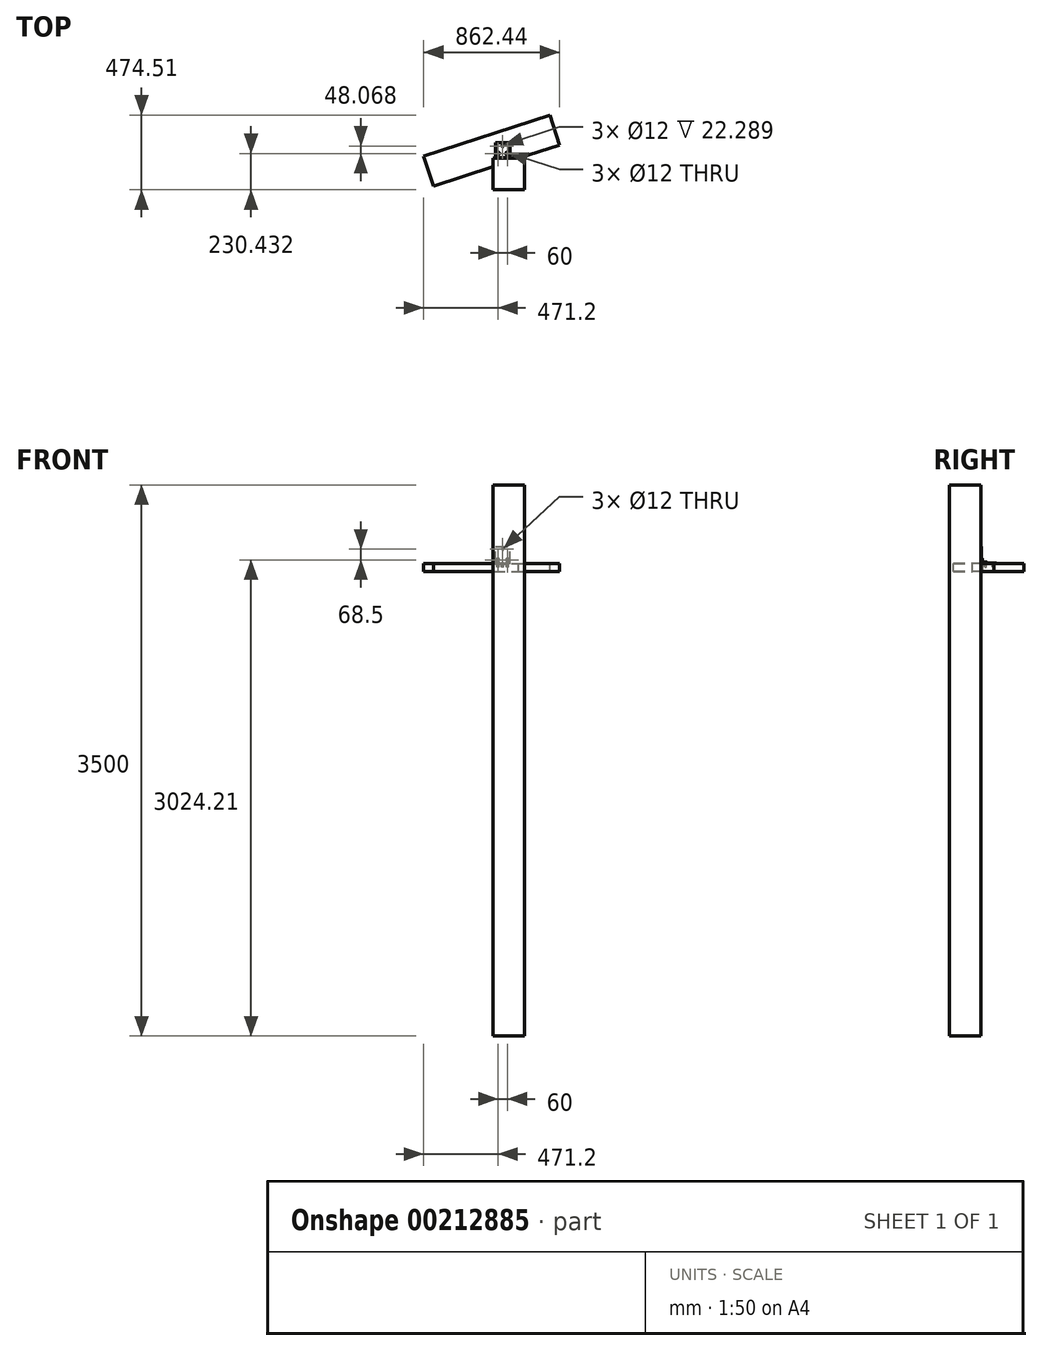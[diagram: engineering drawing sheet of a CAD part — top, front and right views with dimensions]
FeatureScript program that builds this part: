
annotation { "Feature Type Name" : "Feature", "Feature Type Description" : "" }
export const myFeature = defineFeature(function(context is Context, id is Id, definition is map)
    precondition{}
    {
        {
            var Q0;
            Q0=qCreatedBy(makeId("Top.planeOp"),FACE);
            var sketch = newSketch(context, id + "F0", { "sketchPlane" : qUnion([Q0])});
            skLineSegment(sketch, "E0.bottom", {"start": v(-100, 100) * mm, "end": v(100, 100) * mm});
            skLineSegment(sketch, "E0.top", {"start": v(-100, -100) * mm, "end": v(100, -100) * mm});
            skLineSegment(sketch, "E0.left", {"start": v(-100, 100) * mm, "end": v(-100, -100) * mm});
            skLineSegment(sketch, "E0.right", {"start": v(100, 100) * mm, "end": v(100, -100) * mm});
            skPoint(sketch, "E0.middle", {"position": v(0, 0) * mm});
            skSolve(sketch);
        }
        {
            var Q0;
            Q0 = qSketchRegion(id + "F0", true);
            extrude(context, id + "F1", {"entities" : qUnion([Q0]), "depth" : 3000 * mm, "offsetDistance" : 25 * mm});
        }
        {
            var Q0;
            Q0=makeQuery(id+"F1.opExtrude","CAP_FACE",FACE,{"disambiguationData":[OSD([sQuery(id+"F0.wireOp",EDGE,"E0.bottom"),sQuery(id+"F0.wireOp",EDGE,"E0.top"),sQuery(id+"F0.wireOp",EDGE,"E0.left"),sQuery(id+"F0.wireOp",EDGE,"E0.right")])],"isStart":false});
            var sketch = newSketch(context, id + "F2", { "sketchPlane" : qUnion([Q0])});
            skLineSegment(sketch, "E1", {"start": v(-479.4, -75.85) * mm, "end": v(-100, 47.43) * mm});
            skLineSegment(sketch, "E2", {"start": v(-100, 100) * mm, "end": v(100, 100) * mm});
            skLineSegment(sketch, "E3", {"start": v(-100, 100) * mm, "end": v(-100, 47.43) * mm});
            skLineSegment(sketch, "E4", {"start": v(-541.2, 114.37) * mm, "end": v(-479.4, -75.85) * mm});
            skLineSegment(sketch, "E5", {"start": v(259.44, 374.5) * mm, "end": v(321.24, 184.3) * mm});
            skLineSegment(sketch, "E6.trimOffspring", {"start": v(61.8, 100) * mm, "end": v(321.24, 184.3) * mm});
            skLineSegment(sketch, "E7", {"start": v(-541.2, 114.37) * mm, "end": v(259.44, 374.5) * mm});
            skSolve(sketch);
        }
        {
            var Q0;
            Q0 = qSketchRegion(id + "F2", true);
            extrude(context, id + "F3", {"entities" : qUnion([Q0]), "oppositeDirection" : true, "depth" : 50 * mm, "offsetDistance" : 25 * mm});
        }
        {
            var Q0;
            Q0=makeQuery(id+"F1.opExtrude","CAP_FACE",FACE,{"disambiguationData":[OSD([sQuery(id+"F0.wireOp",EDGE,"E0.bottom"),sQuery(id+"F0.wireOp",EDGE,"E0.top"),sQuery(id+"F0.wireOp",EDGE,"E0.left"),sQuery(id+"F0.wireOp",EDGE,"E0.right")])],"isStart":false});
            extrude(context, id + "F4", {"entities" : qUnion([Q0]), "operationType" : NewBodyOperationType.ADD, "depth" : 500 * mm, "offsetDistance" : 25 * mm});
        }
        {
            var Q0;
            {var subQ0=sQuery(id+"F0.wireOp",EDGE,"E0.bottom");Q0=makeQuery(id+"F4.boolean.opBoolean","MERGE",FACE,{"derivedFrom":[makeQuery(id+"F1.opExtrude","SWEPT_FACE",FACE,{"disambiguationData":[OSD([subQ0])]}),makeQuery(id+"F4.opExtrude","SWEPT_FACE",FACE,{"disambiguationData":[OSD([subQ0])]})]});}
            var sketch = newSketch(context, id + "F5", { "sketchPlane" : qUnion([Q0])});
            skLineSegment(sketch, "E8.bottom", {"start": v(85, 2999.21) * mm, "end": v(-5, 2999.21) * mm});
            skLineSegment(sketch, "E8.top", {"start": v(85, 3107.71) * mm, "end": v(-5, 3107.71) * mm});
            skLineSegment(sketch, "E8.right", {"start": v(-5, 2999.21) * mm, "end": v(-5, 3107.71) * mm});
            skLineSegment(sketch, "E9.bottom", {"start": v(85, 2999.21) * mm, "end": v(-31.61, 2999.21) * mm});
            skLineSegment(sketch, "E9.left", {"start": v(85, 2999.21) * mm, "end": v(85, 3107.71) * mm});
            skPoint(sketch, "E10.orphan", {"position": v(-31.61, 3107.71) * mm});
            skCircle(sketch, "E11", {"center": v(70, 3024.21) * mm, "radius": 6 * mm});
            skCircle(sketch, "E12", {"center": v(10, 3024.21) * mm, "radius": 6 * mm});
            skCircle(sketch, "E13", {"center": v(40, 3092.71) * mm, "radius": 6 * mm});
            skSolve(sketch);
        }
        {
            var Q0;
            Q0 = qSketchRegion(id + "F5", true);
            extrude(context, id + "F6", {"entities" : qUnion([Q0]), "depth" : 2.5 * mm, "offsetDistance" : 25 * mm});
        }
        {
            var Q0;
            Q0=makeQuery(id+"F6.opExtrude","CAP_FACE",FACE,{"disambiguationData":[OSD([sQuery(id+"F5.wireOp",EDGE,"E8.right"),sQuery(id+"F5.wireOp",EDGE,"E9.bottom"),sQuery(id+"F5.wireOp",EDGE,"E8.top"),sQuery(id+"F5.wireOp",EDGE,"E9.left"),sQuery(id+"F5.wireOp",EDGE,"E11"),sQuery(id+"F5.wireOp",EDGE,"E12"),sQuery(id+"F5.wireOp",EDGE,"E13")])],"isStart":false});
            var sketch = newSketch(context, id + "F7", { "sketchPlane" : qUnion([Q0])});
            skLineSegment(sketch, "E14.bottom", {"start": v(85, 3000.21) * mm, "end": v(-5, 3000.21) * mm});
            skLineSegment(sketch, "E14.top", {"start": v(85, 3002.71) * mm, "end": v(-5, 3002.71) * mm});
            skLineSegment(sketch, "E14.left", {"start": v(85, 3000.21) * mm, "end": v(85, 3002.71) * mm});
            skLineSegment(sketch, "E14.right", {"start": v(-5, 3000.21) * mm, "end": v(-5, 3002.71) * mm});
            skSolve(sketch);
        }
        {
            var Q0;
            Q0 = qSketchRegion(id + "F7", true);
            extrude(context, id + "F8", {"entities" : qUnion([Q0]), "operationType" : NewBodyOperationType.ADD, "depth" : 96 * mm, "offsetDistance" : 25 * mm});
        }
        {
            var Q0;
            Q0=makeQuery(id+"F8.opExtrude","SWEPT_FACE",FACE,{"disambiguationData":[OSD([sQuery(id+"F7.wireOp",EDGE,"E14.top")])]});
            var sketch = newSketch(context, id + "F9", { "sketchPlane" : qUnion([Q0])});
            skCircle(sketch, "E15", {"center": v(-70, 130.43) * mm, "radius": 6 * mm});
            skCircle(sketch, "E16", {"center": v(-10, 130.43) * mm, "radius": 6 * mm});
            skCircle(sketch, "E17", {"center": v(-40, 178.5) * mm, "radius": 6 * mm});
            skSolve(sketch);
        }
        {
            var Q0;
            Q0 = qSketchRegion(id + "F9", true);
            extrude(context, id + "F10", {"entities" : qUnion([Q0]), "operationType" : NewBodyOperationType.REMOVE, "oppositeDirection" : true, "depth" : 25 * mm, "offsetDistance" : 25 * mm});
        }
        {
            var Q0;
            {var subQ0=sQuery(id+"F5.wireOp",EDGE,"E11");var subQ1=sQuery(id+"F5.wireOp",EDGE,"E8.top");var subQ2=sQuery(id+"F5.wireOp",EDGE,"E9.left");var subQ3=sQuery(id+"F5.wireOp",EDGE,"E8.right");var subQ4=sQuery(id+"F5.wireOp",EDGE,"E12");var subQ5=sQuery(id+"F5.wireOp",EDGE,"E13");Q0=makeQuery(id+"F8.boolean.opBoolean","SPLIT",FACE,{"disambiguationData":[TD([makeQuery(id+"F6.opExtrude","SWEPT_FACE",FACE,{"disambiguationData":[OSD([subQ1])]})])],"derivedFrom":makeQuery(id+"F6.opExtrude","CAP_FACE",FACE,{"disambiguationData":[OSD([subQ3,sQuery(id+"F5.wireOp",EDGE,"E9.bottom"),subQ1,subQ2,subQ0,subQ4,subQ5])],"isStart":false})});}
            var sketch = newSketch(context, id + "F11", { "sketchPlane" : qUnion([Q0])});
            skCircle(sketch, "E18", {"center": v(10, 3024.21) * mm, "radius": 10 * mm});
            skCircle(sketch, "E19", {"center": v(70, 3024.21) * mm, "radius": 10 * mm});
            skSolve(sketch);
        }
        {
            var Q0;
            Q0 = qSketchRegion(id + "F11", true);
            extrude(context, id + "F12", {"entities" : qUnion([Q0]), "depth" : 3 * mm, "offsetDistance" : 25 * mm});
        }
        {
            var Q0;
            Q0=makeQuery(id+"F12.opExtrude","CAP_FACE",FACE,{"disambiguationData":[OSD([sQuery(id+"F11.wireOp",EDGE,"E18")])],"isStart":false});
            var sketch = newSketch(context, id + "F13", { "sketchPlane" : qUnion([Q0])});
            skCircle(sketch, "E20.cCircle", {"center": v(10, 3024.21) * mm, "radius": 8 * mm, "construction": true});
            skLineSegment(sketch, "E20.0", {"start": v(12.07, 3033.21) * mm, "end": v(18.83, 3026.92) * mm});
            skLineSegment(sketch, "E20.1", {"start": v(18.83, 3026.92) * mm, "end": v(16.76, 3017.92) * mm});
            skLineSegment(sketch, "E20.2", {"start": v(16.76, 3017.92) * mm, "end": v(7.93, 3015.2) * mm});
            skLineSegment(sketch, "E20.3", {"start": v(7.93, 3015.2) * mm, "end": v(1.17, 3021.5) * mm});
            skLineSegment(sketch, "E20.4", {"start": v(1.17, 3021.5) * mm, "end": v(3.24, 3030.5) * mm});
            skLineSegment(sketch, "E20.5", {"start": v(3.24, 3030.5) * mm, "end": v(12.07, 3033.21) * mm});
            skPoint(sketch, "E20.0.midPoint", {"position": v(15.45, 3030.07) * mm});
            skSolve(sketch);
        }
        {
            var Q0;
            Q0 = qSketchRegion(id + "F13", true);
            extrude(context, id + "F14", {"entities" : qUnion([Q0]), "depth" : 5 * mm, "offsetDistance" : 25 * mm});
        }
        {
            var Q0;
            Q0=makeQuery(id+"F8.opExtrude","SWEPT_FACE",FACE,{"disambiguationData":[OSD([sQuery(id+"F7.wireOp",EDGE,"E14.top")])]});
            var sketch = newSketch(context, id + "F15", { "sketchPlane" : qUnion([Q0])});
            skCircle(sketch, "E21", {"center": v(-10, 130.43) * mm, "radius": 10 * mm});
            skCircle(sketch, "E22", {"center": v(-70, 130.43) * mm, "radius": 10 * mm});
            skSolve(sketch);
        }
        {
            var Q0;
            Q0 = qSketchRegion(id + "F15", true);
            extrude(context, id + "F16", {"entities" : qUnion([Q0]), "depth" : 3 * mm, "offsetDistance" : 25 * mm});
        }
        {
            var Q0;
            Q0=makeQuery(id+"F16.opExtrude","CAP_FACE",FACE,{"disambiguationData":[OSD([sQuery(id+"F15.wireOp",EDGE,"E22")])],"isStart":false});
            var sketch = newSketch(context, id + "F17", { "sketchPlane" : qUnion([Q0])});
            skCircle(sketch, "E23.cCircle", {"center": v(-70, 130.43) * mm, "radius": 8 * mm, "construction": true});
            skLineSegment(sketch, "E23.0", {"start": v(-77.93, 135.18) * mm, "end": v(-69.86, 139.67) * mm});
            skLineSegment(sketch, "E23.1", {"start": v(-69.86, 139.67) * mm, "end": v(-61.93, 134.92) * mm});
            skLineSegment(sketch, "E23.2", {"start": v(-61.93, 134.92) * mm, "end": v(-62.07, 125.69) * mm});
            skLineSegment(sketch, "E23.3", {"start": v(-62.07, 125.69) * mm, "end": v(-70.14, 121.2) * mm});
            skLineSegment(sketch, "E23.4", {"start": v(-70.14, 121.2) * mm, "end": v(-78.07, 125.94) * mm});
            skLineSegment(sketch, "E23.5", {"start": v(-78.07, 125.94) * mm, "end": v(-77.93, 135.18) * mm});
            skPoint(sketch, "E23.0.midPoint", {"position": v(-73.9, 137.42) * mm});
            skSolve(sketch);
        }
        {
            var Q0;
            Q0 = qSketchRegion(id + "F17", true);
            extrude(context, id + "F18", {"entities" : qUnion([Q0]), "depth" : 5 * mm, "offsetDistance" : 25 * mm});
        }
        {
            var Q0;
            Q0=makeQuery(id+"F16.opExtrude","CAP_FACE",FACE,{"disambiguationData":[OSD([sQuery(id+"F15.wireOp",EDGE,"E21")])],"isStart":false});
            var sketch = newSketch(context, id + "F19", { "sketchPlane" : qUnion([Q0])});
            skCircle(sketch, "E24.cCircle", {"center": v(-10, 130.43) * mm, "radius": 8 * mm, "construction": true});
            skLineSegment(sketch, "E24.0", {"start": v(-19.16, 131.64) * mm, "end": v(-13.54, 138.97) * mm});
            skLineSegment(sketch, "E24.1", {"start": v(-13.54, 138.97) * mm, "end": v(-4.38, 137.76) * mm});
            skLineSegment(sketch, "E24.2", {"start": v(-4.38, 137.76) * mm, "end": v(-0.84, 129.23) * mm});
            skLineSegment(sketch, "E24.3", {"start": v(-0.84, 129.23) * mm, "end": v(-6.46, 121.9) * mm});
            skLineSegment(sketch, "E24.4", {"start": v(-6.46, 121.9) * mm, "end": v(-15.62, 123.1) * mm});
            skLineSegment(sketch, "E24.5", {"start": v(-15.62, 123.1) * mm, "end": v(-19.16, 131.64) * mm});
            skPoint(sketch, "E24.0.midPoint", {"position": v(-16.35, 135.3) * mm});
            skSolve(sketch);
        }
        {
            var Q0;
            Q0 = qSketchRegion(id + "F19", true);
            extrude(context, id + "F20", {"entities" : qUnion([Q0]), "depth" : 5 * mm, "offsetDistance" : 25 * mm});
        }
        {
            var Q0;
            Q0=makeQuery(id+"F12.opExtrude","CAP_FACE",FACE,{"disambiguationData":[OSD([sQuery(id+"F11.wireOp",EDGE,"E19")])],"isStart":false});
            var sketch = newSketch(context, id + "F21", { "sketchPlane" : qUnion([Q0])});
            skCircle(sketch, "E25.cCircle", {"center": v(70, 3024.21) * mm, "radius": 8 * mm, "construction": true});
            skLineSegment(sketch, "E25.0", {"start": v(60.8, 3023.42) * mm, "end": v(64.72, 3031.79) * mm});
            skLineSegment(sketch, "E25.1", {"start": v(64.72, 3031.79) * mm, "end": v(73.92, 3032.58) * mm});
            skLineSegment(sketch, "E25.2", {"start": v(73.92, 3032.58) * mm, "end": v(79.2, 3025) * mm});
            skLineSegment(sketch, "E25.3", {"start": v(79.2, 3025) * mm, "end": v(75.28, 3016.63) * mm});
            skLineSegment(sketch, "E25.4", {"start": v(75.28, 3016.63) * mm, "end": v(66.08, 3015.85) * mm});
            skLineSegment(sketch, "E25.5", {"start": v(66.08, 3015.85) * mm, "end": v(60.8, 3023.42) * mm});
            skPoint(sketch, "E25.0.midPoint", {"position": v(62.76, 3027.6) * mm});
            skSolve(sketch);
        }
        {
            var Q0;
            Q0 = qSketchRegion(id + "F21", true);
            extrude(context, id + "F22", {"entities" : qUnion([Q0]), "depth" : 5 * mm, "offsetDistance" : 25 * mm});
        }
    });
